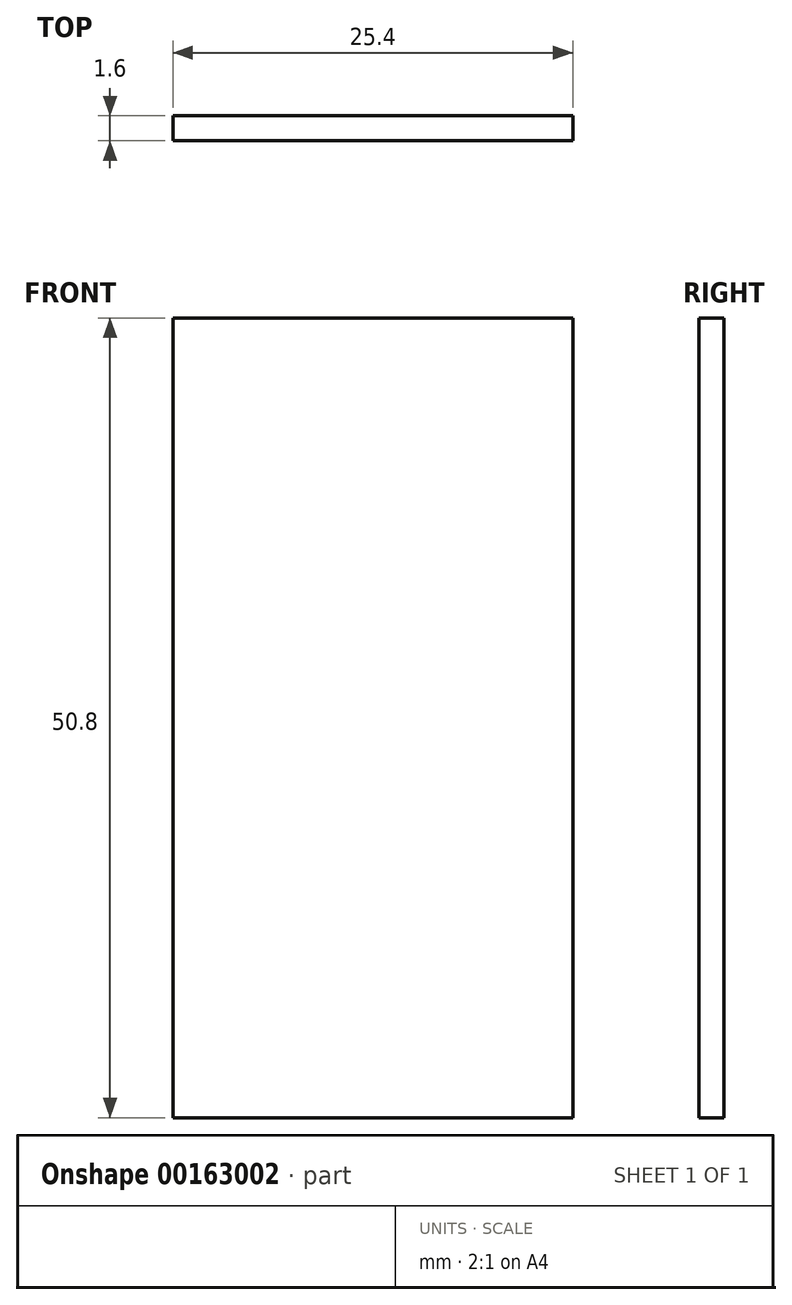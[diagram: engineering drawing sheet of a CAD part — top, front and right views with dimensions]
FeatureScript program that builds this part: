
annotation { "Feature Type Name" : "Feature", "Feature Type Description" : "" }
export const myFeature = defineFeature(function(context is Context, id is Id, definition is map)
    precondition{}
    {
        {
            var Q0;
            Q0=qCreatedBy(makeId("Right.planeOp"),FACE);
            var sketch = newSketch(context, id + "F0", { "sketchPlane" : qUnion([Q0])});
            skLineSegment(sketch, "E0", {"start": v(0, 25.4) * mm, "end": v(-1.6, 25.4) * mm});
            skLineSegment(sketch, "E1", {"start": v(-1.6, 25.4) * mm, "end": v(-1.6, -25.4) * mm});
            skLineSegment(sketch, "E2", {"start": v(0, 25.4) * mm, "end": v(0, -25.4) * mm});
            skLineSegment(sketch, "E3", {"start": v(0, -25.4) * mm, "end": v(-1.6, -25.4) * mm});
            skSolve(sketch);
        }
        {
            var Q0;
            Q0 = qSketchRegion(id + "F0", true);
            extrude(context, id + "F1", {"entities" : qUnion([Q0]), "depth" : 25.4 * mm});
        }
    });
